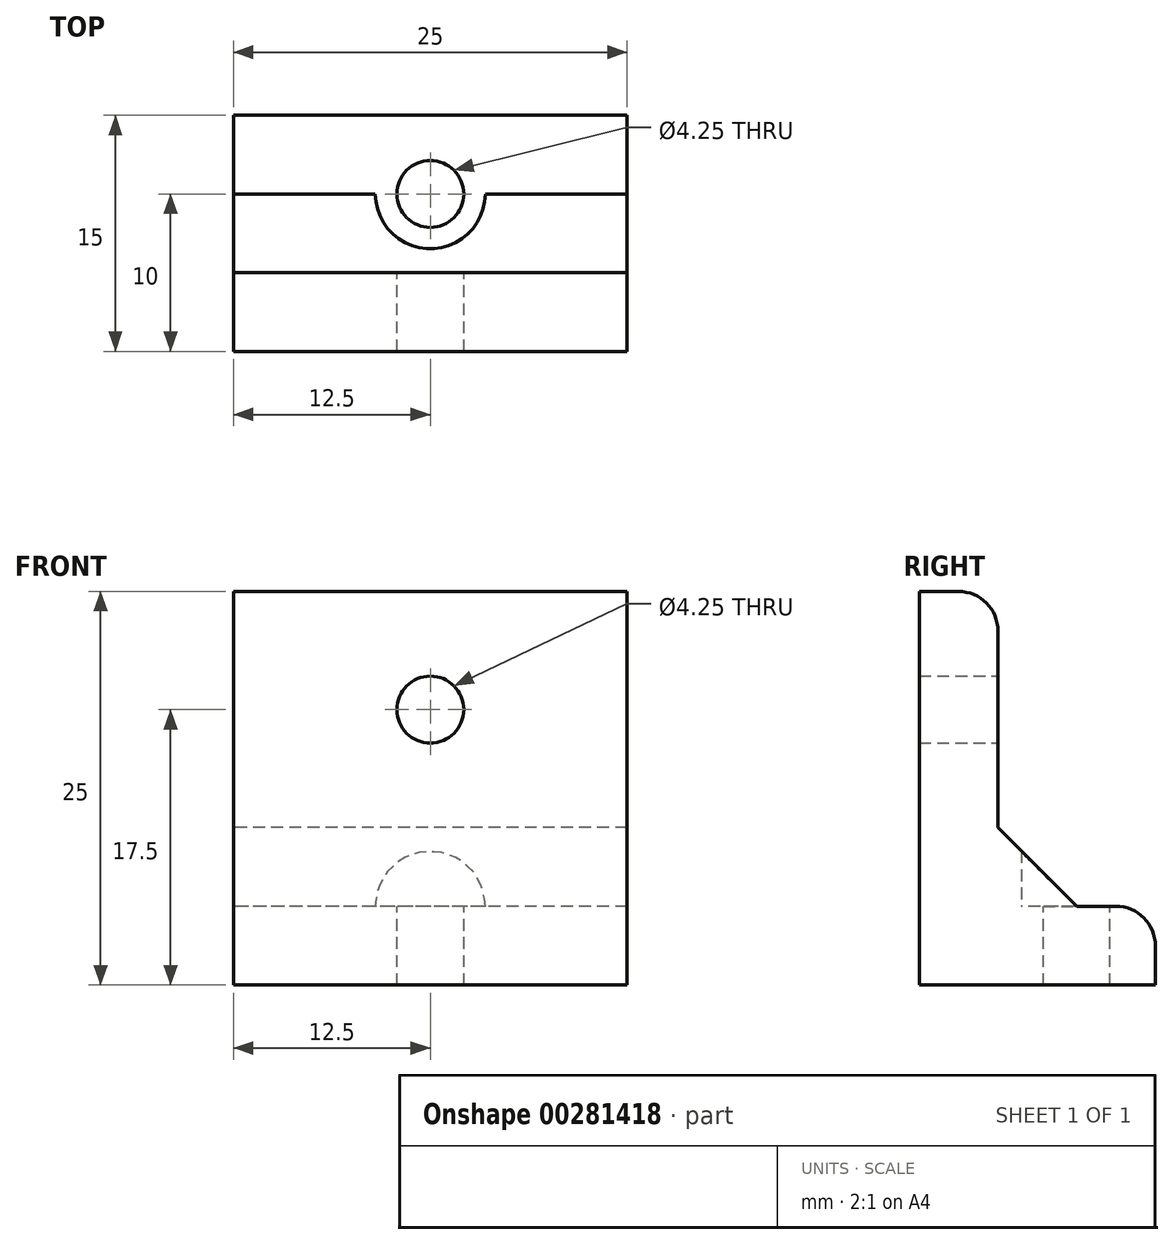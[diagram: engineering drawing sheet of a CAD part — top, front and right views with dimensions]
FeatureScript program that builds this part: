
annotation { "Feature Type Name" : "Feature", "Feature Type Description" : "" }
export const myFeature = defineFeature(function(context is Context, id is Id, definition is map)
    precondition{}
    {
        {
            var Q0;
            Q0=qCreatedBy(makeId("Right.planeOp"),FACE);
            var sketch = newSketch(context, id + "F0", { "sketchPlane" : qUnion([Q0])});
            skLineSegment(sketch, "E0", {"start": v(0, 25) * mm, "end": v(0, 0) * mm});
            skLineSegment(sketch, "E1", {"start": v(0, 0) * mm, "end": v(15, 0) * mm});
            skLineSegment(sketch, "E2", {"start": v(15, 0) * mm, "end": v(15, 5) * mm});
            skLineSegment(sketch, "E3", {"start": v(15, 5) * mm, "end": v(10, 5) * mm});
            skLineSegment(sketch, "E4", {"start": v(10, 5) * mm, "end": v(5, 10) * mm});
            skLineSegment(sketch, "E5", {"start": v(5, 10) * mm, "end": v(5, 25) * mm});
            skLineSegment(sketch, "E6", {"start": v(5, 25) * mm, "end": v(0, 25) * mm});
            skSolve(sketch);
        }
        {
            var Q0;
            Q0=qSketchRegion(id+"F0",true);
            extrude(context, id + "F1", {"entities" : qUnion([Q0]), "endBound" : BoundingType.SYMMETRIC, "depth" : 25 * mm});
        }
        {
            var Q0;
            Q0=makeQuery(id+"F1.opExtrude","SWEPT_FACE",FACE,{"disambiguationData":[OSD([sQuery(id+"F0.wireOp",EDGE,"E3")])]});
            var sketch = newSketch(context, id + "F2", { "sketchPlane" : qUnion([Q0])});
            skCircle(sketch, "E7", {"center": v(0, 10) * mm, "radius": 2.12 * mm});
            skSolve(sketch);
        }
        {
            var Q0;
            Q0=qSketchRegion(id+"F2",true);
            extrude(context, id + "F3", {"entities" : qUnion([Q0]), "operationType" : NewBodyOperationType.REMOVE, "endBound" : BoundingType.THROUGH_ALL, "oppositeDirection" : true, "depth" : 25 * mm});
        }
        {
            var Q0;
            Q0=makeQuery(id+"F1.opExtrude","SWEPT_FACE",FACE,{"disambiguationData":[OSD([sQuery(id+"F0.wireOp",EDGE,"E5")])]});
            var sketch = newSketch(context, id + "F4", { "sketchPlane" : qUnion([Q0])});
            skCircle(sketch, "E8", {"center": v(0, 17.5) * mm, "radius": 2.12 * mm});
            skPoint(sketch, "E8.centerSnap0", {"position": v(0, 25) * mm});
            skSolve(sketch);
        }
        {
            var Q0;
            Q0=qSketchRegion(id+"F4",true);
            extrude(context, id + "F5", {"entities" : qUnion([Q0]), "operationType" : NewBodyOperationType.REMOVE, "endBound" : BoundingType.THROUGH_ALL, "oppositeDirection" : true, "depth" : 25 * mm});
        }
        {
            var Q0;
            Q0=makeQuery(id+"F1.opExtrude","SWEPT_EDGE",EDGE,{"disambiguationData":[OSD([sQuery(id+"F0.wireOp",EDGE,"E2"),sQuery(id+"F0.wireOp",EDGE,"E3")])]});
            var Q1;
            Q1=makeQuery(id+"F1.opExtrude","SWEPT_EDGE",EDGE,{"disambiguationData":[OSD([sQuery(id+"F0.wireOp",EDGE,"E5"),sQuery(id+"F0.wireOp",EDGE,"E6")])]});
            fillet(context, id + "F6", {"entities" : qUnion([Q0, Q1]), "radius" : 2.5 * mm, "tangentPropagation" : true, "allowEdgeOverflow" : false});
        }
        {
            var Q0;
            Q0=makeQuery(id+"F3.boolean.opBoolean","COPY",FACE,{"derivedFrom":makeQuery(id+"F3.opExtrude","CAP_FACE",FACE,{"disambiguationData":[OSD([sQuery(id+"F2.wireOp",EDGE,"E7")])],"isStart":true})});
            var sketch = newSketch(context, id + "F7", { "sketchPlane" : qUnion([Q0])});
            skCircle(sketch, "E9", {"center": v(0, -10) * mm, "radius": 3.5 * mm});
            skSolve(sketch);
        }
        {
            var Q0;
            Q0=qSketchRegion(id+"F7",true);
            extrude(context, id + "F8", {"entities" : qUnion([Q0]), "operationType" : NewBodyOperationType.REMOVE, "endBound" : BoundingType.THROUGH_ALL, "oppositeDirection" : true, "depth" : 25 * mm});
        }
    });
